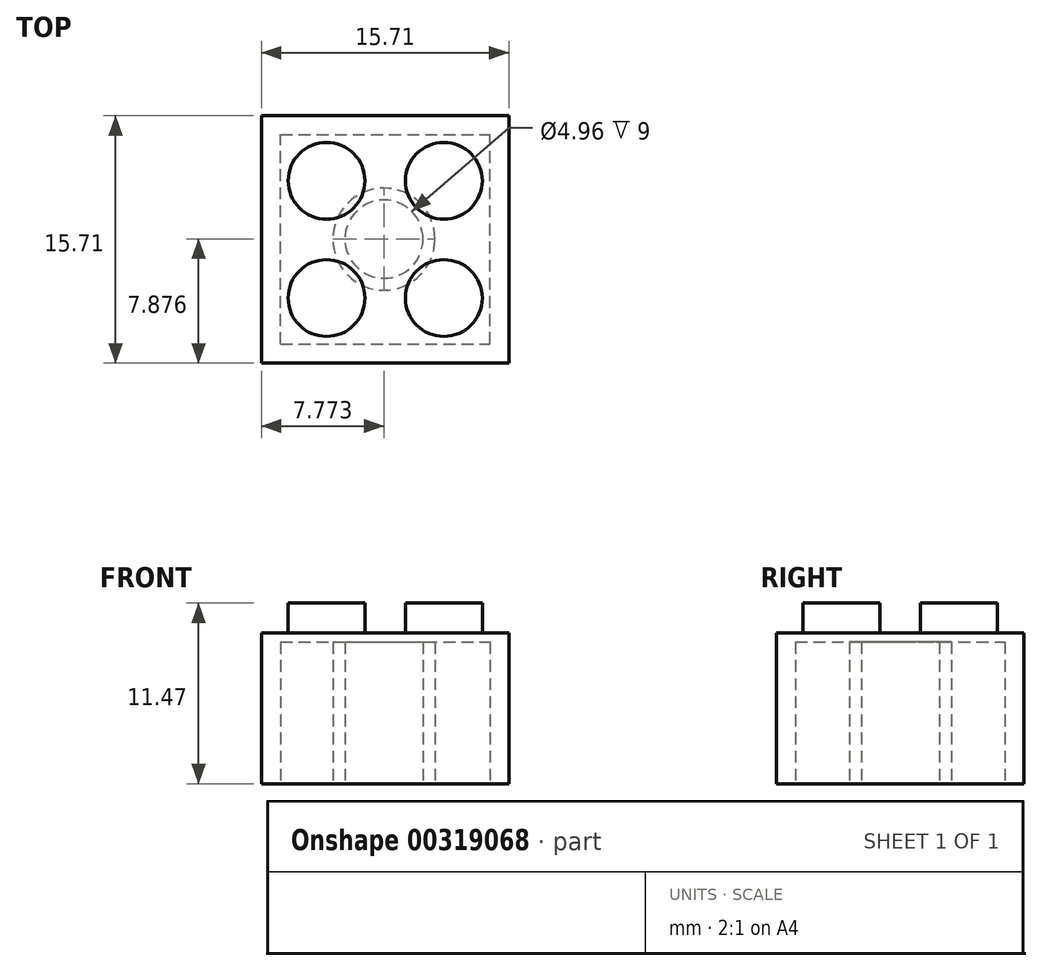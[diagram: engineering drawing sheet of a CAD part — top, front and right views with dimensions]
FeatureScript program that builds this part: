
annotation { "Feature Type Name" : "Feature", "Feature Type Description" : "" }
export const myFeature = defineFeature(function(context is Context, id is Id, definition is map)
    precondition{}
    {
        {
            var Q0;
            Q0=qCreatedBy(makeId("Front.planeOp"),FACE);
            var sketch = newSketch(context, id + "F0", { "sketchPlane" : qUnion([Q0])});
            skLineSegment(sketch, "E0.bottom", {"start": v(-7.1, 8.36) * mm, "end": v(8.62, 8.36) * mm});
            skLineSegment(sketch, "E0.top", {"start": v(-7.1, -1.2) * mm, "end": v(8.62, -1.2) * mm});
            skLineSegment(sketch, "E0.left", {"start": v(-7.1, 8.36) * mm, "end": v(-7.1, -1.2) * mm});
            skLineSegment(sketch, "E0.right", {"start": v(8.62, 8.36) * mm, "end": v(8.62, -1.2) * mm});
            skSolve(sketch);
        }
        {
            var Q0;
            Q0=makeQuery(id+"F0.imprint","IMPRINT",FACE,{"disambiguationData":[TD([[makeQuery(id+"F0.imprint","IMPRINT",EDGE,{"derivedFrom":sQuery(id+"F0.wireOp",EDGE,"E0.bottom")}),-1.0]])]});
            extrude(context, id + "F1", {"entities" : qUnion([Q0]), "depth" : 15.71 * mm});
        }
        {
            var Q0;
            Q0=makeQuery(id+"F1.opExtrude","SWEPT_FACE",FACE,{"disambiguationData":[OSD([sQuery(id+"F0.wireOp",EDGE,"E0.bottom")])]});
            var sketch = newSketch(context, id + "F2", { "sketchPlane" : qUnion([Q0])});
            skCircle(sketch, "E1", {"center": v(-2.96, -4.13) * mm, "radius": 2.44 * mm});
            skCircle(sketch, "E2", {"center": v(-2.96, -11.58) * mm, "radius": 2.44 * mm});
            skCircle(sketch, "E3", {"center": v(4.49, -4.13) * mm, "radius": 2.44 * mm});
            skCircle(sketch, "E4", {"center": v(4.49, -11.58) * mm, "radius": 2.44 * mm});
            skSolve(sketch);
        }
        {
            var Q0;
            Q0=makeQuery(id+"F2.imprint","IMPRINT",FACE,{"disambiguationData":[TD([[makeQuery(id+"F2.imprint","IMPRINT",EDGE,{"derivedFrom":sQuery(id+"F2.wireOp",EDGE,"E4")}),1.0]])]});
            var Q1;
            Q1=makeQuery(id+"F2.imprint","IMPRINT",FACE,{"disambiguationData":[TD([[makeQuery(id+"F2.imprint","IMPRINT",EDGE,{"derivedFrom":sQuery(id+"F2.wireOp",EDGE,"E2")}),1.0]])]});
            var Q2;
            Q2=makeQuery(id+"F2.imprint","IMPRINT",FACE,{"disambiguationData":[TD([[makeQuery(id+"F2.imprint","IMPRINT",EDGE,{"derivedFrom":sQuery(id+"F2.wireOp",EDGE,"E1")}),1.0]])]});
            var Q3;
            Q3=makeQuery(id+"F2.imprint","IMPRINT",FACE,{"disambiguationData":[TD([[makeQuery(id+"F2.imprint","IMPRINT",EDGE,{"derivedFrom":sQuery(id+"F2.wireOp",EDGE,"E3")}),1.0]])]});
            extrude(context, id + "F3", {"entities" : qUnion([Q0, Q1, Q2, Q3]), "operationType" : NewBodyOperationType.ADD, "depth" : 1.9 * mm});
        }
        {
            var Q0;
            Q0=makeQuery(id+"F1.opExtrude","SWEPT_FACE",FACE,{"disambiguationData":[OSD([sQuery(id+"F0.wireOp",EDGE,"E0.top")])]});
            var sketch = newSketch(context, id + "F4", { "sketchPlane" : qUnion([Q0])});
            skCircle(sketch, "E5", {"center": v(0.68, 7.83) * mm, "radius": 3.24 * mm});
            skCircle(sketch, "E6", {"center": v(-3.65, 12.27) * mm, "radius": 2 * mm});
            skCircle(sketch, "E7", {"center": v(5.2, 12.32) * mm, "radius": 2 * mm});
            skCircle(sketch, "E8", {"center": v(-3.65, 3.42) * mm, "radius": 2 * mm});
            skCircle(sketch, "E9", {"center": v(5.2, 3.47) * mm, "radius": 2 * mm});
            skLineSegment(sketch, "E10.bottom", {"start": v(-5.88, 14.5) * mm, "end": v(7.4, 14.5) * mm});
            skLineSegment(sketch, "E10.top", {"start": v(-5.88, 1.21) * mm, "end": v(7.4, 1.21) * mm});
            skLineSegment(sketch, "E10.left", {"start": v(-5.88, 14.5) * mm, "end": v(-5.88, 1.21) * mm});
            skLineSegment(sketch, "E10.right", {"start": v(7.4, 14.5) * mm, "end": v(7.4, 1.21) * mm});
            skSolve(sketch);
        }
        {
            var Q0;
            Q0=makeQuery(id+"F4.imprint","IMPRINT",FACE,{"disambiguationData":[TD([[makeQuery(id+"F4.imprint","IMPRINT",EDGE,{"derivedFrom":sQuery(id+"F4.wireOp",EDGE,"E8")}),1.0]])]});
            var Q1;
            Q1=makeQuery(id+"F4.imprint","IMPRINT",FACE,{"disambiguationData":[TD([[makeQuery(id+"F4.imprint","IMPRINT",EDGE,{"derivedFrom":sQuery(id+"F4.wireOp",EDGE,"E6")}),1.0]])]});
            var Q2;
            Q2=makeQuery(id+"F4.imprint","IMPRINT",FACE,{"disambiguationData":[TD([[makeQuery(id+"F4.imprint","IMPRINT",EDGE,{"derivedFrom":sQuery(id+"F4.wireOp",EDGE,"E7")}),1.0]])]});
            var Q3;
            Q3=makeQuery(id+"F4.imprint","IMPRINT",FACE,{"disambiguationData":[TD([[makeQuery(id+"F4.imprint","IMPRINT",EDGE,{"derivedFrom":sQuery(id+"F4.wireOp",EDGE,"E9")}),1.0]])]});
            var Q4;
            Q4=makeQuery(id+"F4.imprint","IMPRINT",FACE,{"disambiguationData":[TD([[makeQuery(id+"F4.imprint","IMPRINT",EDGE,{"derivedFrom":sQuery(id+"F4.wireOp",EDGE,"E5")}),-1.0]])]});
            extrude(context, id + "F5", {"entities" : qUnion([Q0, Q1, Q2, Q3, Q4]), "operationType" : NewBodyOperationType.REMOVE, "oppositeDirection" : true, "depth" : 9 * mm});
        }
        {
            var Q0;
            Q0=makeQuery(id+"F5.boolean.opBoolean","SPLIT",FACE,{"disambiguationData":[TD([makeQuery(id+"F5.opExtrude","SWEPT_FACE",FACE,{"disambiguationData":[OSD([sQuery(id+"F4.wireOp",EDGE,"E5")])]})])],"derivedFrom":makeQuery(id+"F1.opExtrude","SWEPT_FACE",FACE,{"disambiguationData":[OSD([sQuery(id+"F0.wireOp",EDGE,"E0.top")])]})});
            var sketch = newSketch(context, id + "F6", { "sketchPlane" : qUnion([Q0])});
            skCircle(sketch, "E11", {"center": v(0.68, 7.83) * mm, "radius": 2.48 * mm});
            skSolve(sketch);
        }
        {
            var Q0;
            Q0=makeQuery(id+"F6.imprint","IMPRINT",FACE,{"disambiguationData":[TD([[makeQuery(id+"F6.imprint","IMPRINT",EDGE,{"derivedFrom":sQuery(id+"F6.wireOp",EDGE,"E11")}),1.0]])]});
            extrude(context, id + "F7", {"entities" : qUnion([Q0]), "operationType" : NewBodyOperationType.REMOVE, "oppositeDirection" : true, "depth" : 9 * mm});
        }
    });
